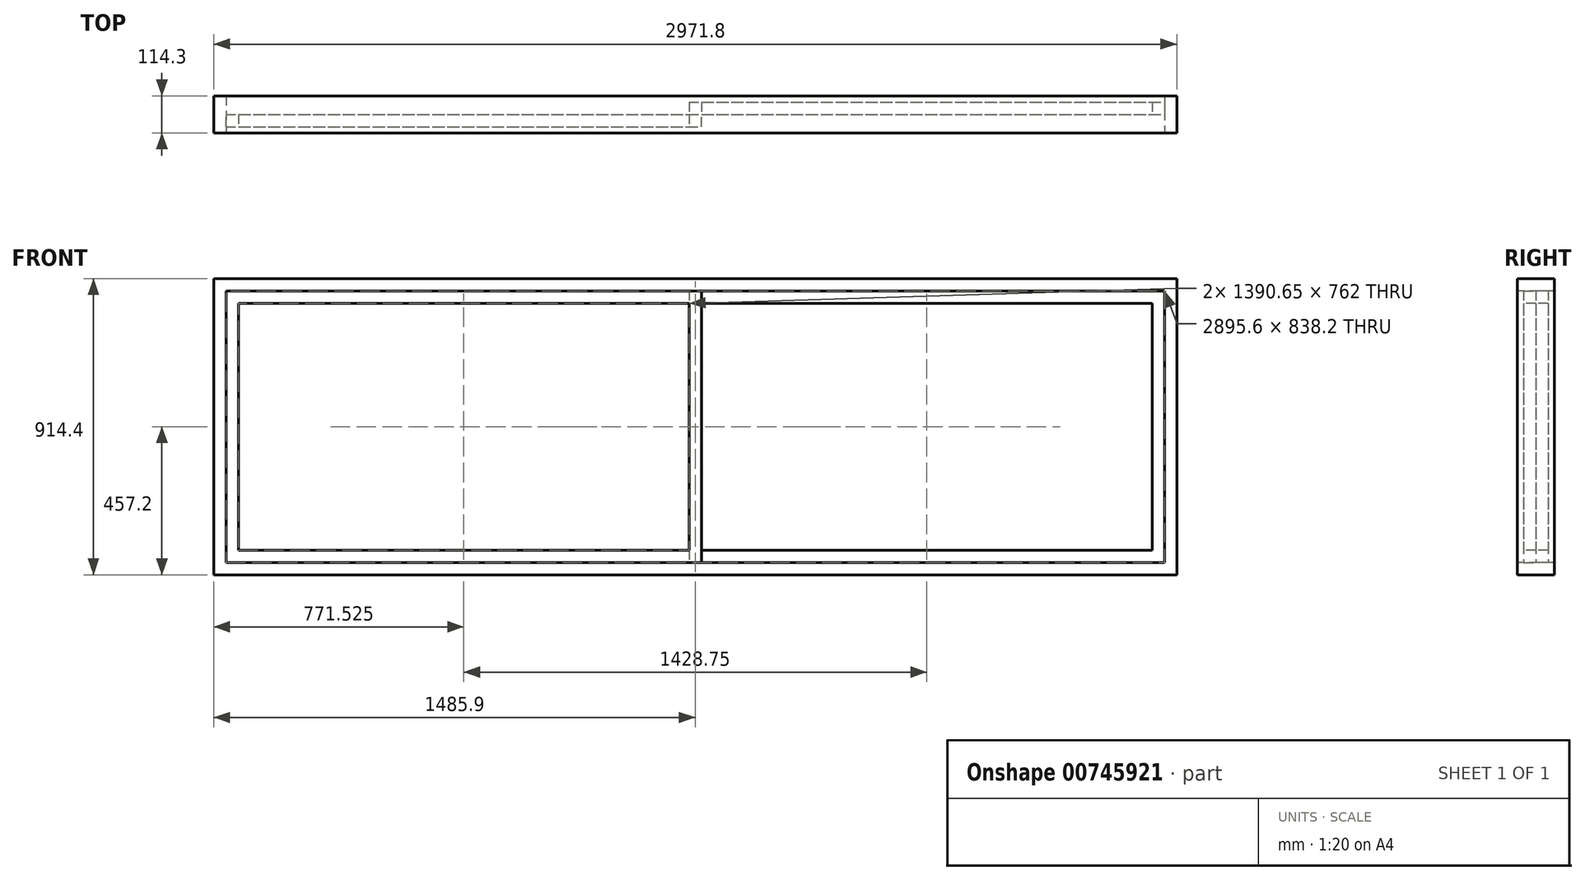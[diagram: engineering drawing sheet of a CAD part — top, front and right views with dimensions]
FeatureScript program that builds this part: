
annotation { "Feature Type Name" : "Feature", "Feature Type Description" : "" }
export const myFeature = defineFeature(function(context is Context, id is Id, definition is map)
    precondition{}
    {
        {
            var Q0;
            Q0=qCreatedBy(makeId("Front.planeOp"),FACE);
            var sketch = newSketch(context, id + "F0", { "sketchPlane" : qUnion([Q0])});
            skLineSegment(sketch, "E0.bottom", {"start": v(-1485.9, 457.2) * mm, "end": v(1485.9, 457.2) * mm});
            skLineSegment(sketch, "E0.top", {"start": v(-1485.9, -457.2) * mm, "end": v(1485.9, -457.2) * mm});
            skLineSegment(sketch, "E0.left", {"start": v(-1485.9, 457.2) * mm, "end": v(-1485.9, -457.2) * mm});
            skLineSegment(sketch, "E0.right", {"start": v(1485.9, 457.2) * mm, "end": v(1485.9, -457.2) * mm});
            skLineSegment(sketch, "E1", {"start": v(0, 457.2) * mm, "end": v(0, 0) * mm, "construction": true});
            skLineSegment(sketch, "E2", {"start": v(0, 0) * mm, "end": v(-1485.9, 0) * mm, "construction": true});
            skSolve(sketch);
        }
        {
            var Q0;
            Q0=makeQuery(id+"F0.imprint","IMPRINT",FACE,{"disambiguationData":[TD([[makeQuery(id+"F0.imprint","IMPRINT",EDGE,{"derivedFrom":sQuery(id+"F0.wireOp",EDGE,"E0.bottom")}),-1.0]])]});
            extrude(context, id + "F1", {"entities" : qUnion([Q0]), "endBound" : BoundingType.SYMMETRIC, "depth" : 114.3 * mm, "offsetDistance" : 25.4 * mm});
        }
        {
            var Q0;
            Q0=makeQuery(id+"F1.opExtrude","CAP_FACE",FACE,{"disambiguationData":[OSD([sQuery(id+"F0.wireOp",EDGE,"E0.bottom"),sQuery(id+"F0.wireOp",EDGE,"E0.top"),sQuery(id+"F0.wireOp",EDGE,"E0.left"),sQuery(id+"F0.wireOp",EDGE,"E0.right")])],"isStart":false});
            var sketch = newSketch(context, id + "F2", { "sketchPlane" : qUnion([Q0])});
            skLineSegment(sketch, "E3.bottom", {"start": v(-1447.8, 419.1) * mm, "end": v(1447.8, 419.1) * mm});
            skLineSegment(sketch, "E3.top", {"start": v(-1447.8, -419.1) * mm, "end": v(1447.8, -419.1) * mm});
            skLineSegment(sketch, "E3.left", {"start": v(-1447.8, 419.1) * mm, "end": v(-1447.8, -419.1) * mm});
            skLineSegment(sketch, "E3.right", {"start": v(1447.8, 419.1) * mm, "end": v(1447.8, -419.1) * mm});
            skSolve(sketch);
        }
        {
            var Q0;
            Q0=makeQuery(id+"F2.imprint","IMPRINT",FACE,{"disambiguationData":[TD([[makeQuery(id+"F2.imprint","IMPRINT",EDGE,{"derivedFrom":sQuery(id+"F2.wireOp",EDGE,"E3.bottom")}),-1.0]])]});
            extrude(context, id + "F3", {"entities" : qUnion([Q0]), "operationType" : NewBodyOperationType.REMOVE, "endBound" : BoundingType.THROUGH_ALL, "oppositeDirection" : true, "depth" : 25.4 * mm, "offsetDistance" : 25.4 * mm});
        }
        {
            var Q0;
            Q0=qCreatedBy(makeId("Front.planeOp"),FACE);
            var sketch = newSketch(context, id + "F4", { "sketchPlane" : qUnion([Q0])});
            skLineSegment(sketch, "E4.bottom", {"start": v(-1447.8, 419.1) * mm, "end": v(19.05, 419.1) * mm});
            skLineSegment(sketch, "E4.top", {"start": v(-1447.8, -419.1) * mm, "end": v(19.05, -419.1) * mm});
            skLineSegment(sketch, "E4.left", {"start": v(-1447.8, 419.1) * mm, "end": v(-1447.8, -419.1) * mm});
            skLineSegment(sketch, "E4.right", {"start": v(19.05, 419.1) * mm, "end": v(19.05, -419.1) * mm});
            skSolve(sketch);
        }
        {
            var Q0;
            Q0=makeQuery(id+"F4.imprint","IMPRINT",FACE,{"disambiguationData":[TD([[makeQuery(id+"F4.imprint","IMPRINT",EDGE,{"derivedFrom":sQuery(id+"F4.wireOp",EDGE,"E4.bottom")}),-1.0]])]});
            extrude(context, id + "F5", {"entities" : qUnion([Q0]), "depth" : 38.1 * mm, "offsetDistance" : 25.4 * mm});
        }
        {
            var Q0;
            Q0=makeQuery(id+"F5.opExtrude","CAP_FACE",FACE,{"disambiguationData":[OSD([sQuery(id+"F4.wireOp",EDGE,"E4.bottom"),sQuery(id+"F4.wireOp",EDGE,"E4.top"),sQuery(id+"F4.wireOp",EDGE,"E4.left"),sQuery(id+"F4.wireOp",EDGE,"E4.right")])],"isStart":false});
            var sketch = newSketch(context, id + "F6", { "sketchPlane" : qUnion([Q0])});
            skLineSegment(sketch, "E5.bottom", {"start": v(-1409.7, 381) * mm, "end": v(-19.05, 381) * mm});
            skLineSegment(sketch, "E5.top", {"start": v(-1409.7, -381) * mm, "end": v(-19.05, -381) * mm});
            skLineSegment(sketch, "E5.left", {"start": v(-1409.7, 381) * mm, "end": v(-1409.7, -381) * mm});
            skLineSegment(sketch, "E5.right", {"start": v(-19.05, 381) * mm, "end": v(-19.05, -381) * mm});
            skSolve(sketch);
        }
        {
            var Q0;
            Q0=qSketchRegion(id+"F6",true);
            extrude(context, id + "F7", {"entities" : qUnion([Q0]), "operationType" : NewBodyOperationType.REMOVE, "endBound" : BoundingType.THROUGH_ALL, "oppositeDirection" : true, "depth" : 25.4 * mm, "offsetDistance" : 25.4 * mm});
        }
        {
            var Q0;
            Q0=qCreatedBy(makeId("Front.planeOp"),FACE);
            var sketch = newSketch(context, id + "F8", { "sketchPlane" : qUnion([Q0])});
            skLineSegment(sketch, "E6.bottom", {"start": v(-19.05, 419.1) * mm, "end": v(1447.8, 419.1) * mm});
            skLineSegment(sketch, "E6.top", {"start": v(-19.05, -419.1) * mm, "end": v(1447.8, -419.1) * mm});
            skLineSegment(sketch, "E6.left", {"start": v(-19.05, 419.1) * mm, "end": v(-19.05, -419.1) * mm});
            skLineSegment(sketch, "E6.right", {"start": v(1447.8, 419.1) * mm, "end": v(1447.8, -419.1) * mm});
            skSolve(sketch);
        }
        {
            var Q0;
            Q0=qSketchRegion(id+"F8",true);
            extrude(context, id + "F9", {"entities" : qUnion([Q0]), "oppositeDirection" : true, "depth" : 38.1 * mm, "offsetDistance" : 25.4 * mm});
        }
        {
            var Q0;
            Q0=makeQuery(id+"F9.opExtrude","CAP_FACE",FACE,{"disambiguationData":[OSD([sQuery(id+"F8.wireOp",EDGE,"E6.bottom"),sQuery(id+"F8.wireOp",EDGE,"E6.top"),sQuery(id+"F8.wireOp",EDGE,"E6.left"),sQuery(id+"F8.wireOp",EDGE,"E6.right")])],"isStart":true});
            var sketch = newSketch(context, id + "F10", { "sketchPlane" : qUnion([Q0])});
            skLineSegment(sketch, "E7.bottom", {"start": v(19.05, 381) * mm, "end": v(1409.7, 381) * mm});
            skLineSegment(sketch, "E7.top", {"start": v(19.05, -381) * mm, "end": v(1409.7, -381) * mm});
            skLineSegment(sketch, "E7.left", {"start": v(19.05, 381) * mm, "end": v(19.05, -381) * mm});
            skLineSegment(sketch, "E7.right", {"start": v(1409.7, 381) * mm, "end": v(1409.7, -381) * mm});
            skSolve(sketch);
        }
        {
            var Q0;
            Q0=qSketchRegion(id+"F10",true);
            extrude(context, id + "F11", {"entities" : qUnion([Q0]), "operationType" : NewBodyOperationType.REMOVE, "endBound" : BoundingType.THROUGH_ALL, "oppositeDirection" : true, "depth" : 25.4 * mm, "offsetDistance" : 25.4 * mm});
        }
    });
